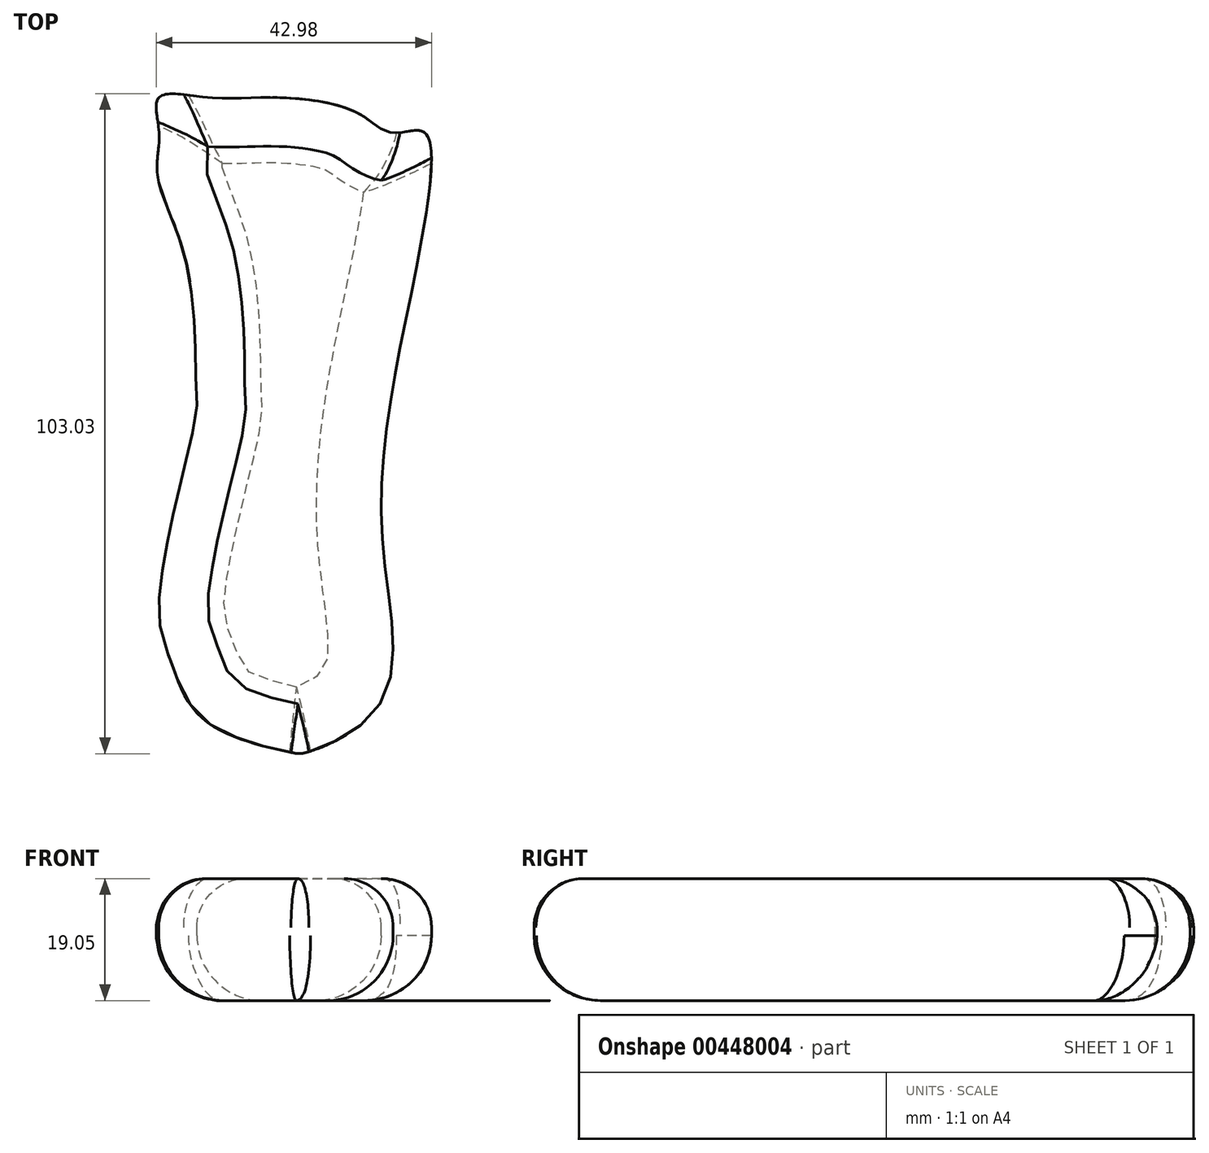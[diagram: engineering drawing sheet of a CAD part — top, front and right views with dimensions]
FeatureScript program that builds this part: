
annotation { "Feature Type Name" : "Feature", "Feature Type Description" : "" }
export const myFeature = defineFeature(function(context is Context, id is Id, definition is map)
    precondition{}
    {
        {
            var Q0;
            Q0=qCreatedBy(makeId("Top.planeOp"),FACE);
            var sketch = newSketch(context, id + "F0", { "sketchPlane" : qUnion([Q0])});
            skFitSpline(sketch, "E0", {"points": [v(-10.22, 16.46) * mm, v(-5.54, 2.07) * mm, v(-4.15, -18.66) * mm, v(-4.15, -20.96) * mm, v(-9.97, -49.4) * mm, v(-8.03, -59.65) * mm, v(-2.47, -68.85) * mm, v(10.77, -73.59) * mm, v(12.92, -73.59) * mm, v(24.57, -65.96) * mm, v(24.93, -40.87) * mm, v(26.55, -16.37) * mm, v(28.92, -4.24) * mm, v(31.21, 7.6) * mm, v(31.52, 23.16) * mm, v(26.55, 23.16) * mm, v(20.92, 26.33) * mm, v(7.5, 28.7) * mm, v(-2.5, 28.7) * mm, v(-9.97, 28.7) * mm, v(-9.97, 23.16) * mm, v(-10.22, 16.46) * mm]});
            skSolve(sketch);
        }
        {
            var Q0;
            Q0 = qSketchRegion(id + "F0", true);
            extrude(context, id + "F1", {"entities" : qUnion([Q0]), "depth" : 19.05 * mm});
        }
        {
            var Q0;
            Q0=makeQuery(id+"F1.opExtrude","CAP_EDGE",EDGE,{"disambiguationData":[OSD([sQuery(id+"F0.wireOp",EDGE,"E0")])],"isStart":true});
            fillet(context, id + "F2", {"entities" : qUnion([Q0]), "radius" : 10.16 * mm, "tangentPropagation" : true, "allowEdgeOverflow" : false});
        }
        {
            var Q0;
            Q0=makeQuery(id+"F1.opExtrude","CAP_EDGE",EDGE,{"disambiguationData":[OSD([sQuery(id+"F0.wireOp",EDGE,"E0")])],"isStart":false});
            fillet(context, id + "F3", {"entities" : qUnion([Q0]), "radius" : 7.62 * mm, "tangentPropagation" : true, "allowEdgeOverflow" : false});
        }
    });
